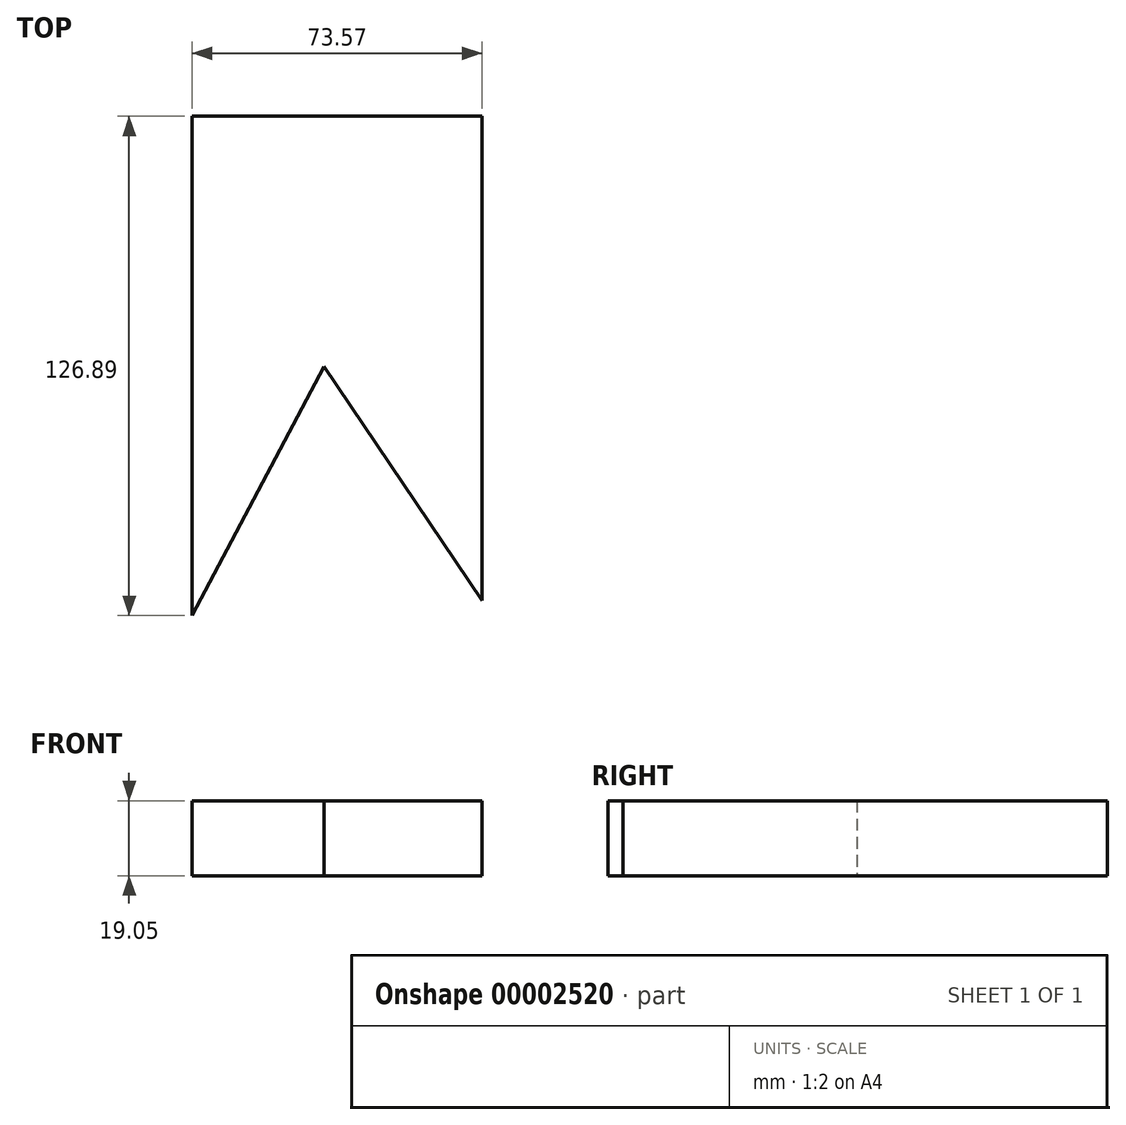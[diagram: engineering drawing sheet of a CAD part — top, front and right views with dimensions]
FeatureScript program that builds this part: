
annotation { "Feature Type Name" : "Feature", "Feature Type Description" : "" }
export const myFeature = defineFeature(function(context is Context, id is Id, definition is map)
    precondition{}
    {
        {
            var Q0;
            Q0=qCreatedBy(makeId("Top.planeOp"),FACE);
            var sketch = newSketch(context, id + "F0", { "sketchPlane" : qUnion([Q0])});
            skLineSegment(sketch, "E0", {"start": v(-237.79, 256.38) * mm, "end": v(-38.32, -319.66) * mm, "construction": true});
            skCircle(sketch, "E1", {"center": v(-237.79, 256.38) * mm, "radius": 22.23 * mm, "construction": true});
            skCircle(sketch, "E2", {"center": v(-38.32, -319.66) * mm, "radius": 22.23 * mm, "construction": true});
            skSolve(sketch);
        }
        {
            var Q0;
            Q0=qCreatedBy(makeId("Top.planeOp"),FACE);
            var sketch = newSketch(context, id + "F1", { "sketchPlane" : qUnion([Q0])});
            skLineSegment(sketch, "E3", {"start": v(-273.6, 236.28) * mm, "end": v(-240.07, 299.53) * mm});
            skLineSegment(sketch, "E4", {"start": v(-240.07, 299.53) * mm, "end": v(-200.03, 240.13) * mm});
            skLineSegment(sketch, "E5", {"start": v(-200.03, 240.13) * mm, "end": v(-200.03, 363.17) * mm});
            skLineSegment(sketch, "E6", {"start": v(-200.03, 363.17) * mm, "end": v(-273.6, 363.17) * mm});
            skLineSegment(sketch, "E7", {"start": v(-273.6, 363.17) * mm, "end": v(-273.6, 236.28) * mm});
            skSolve(sketch);
        }
        {
            var Q0;
            Q0 = qSketchRegion(id + "F1", true);
            extrude(context, id + "F2", {"entities" : qUnion([Q0]), "depth" : 19.05 * mm});
        }
        {
            var Q0;
            Q0=qCreatedBy(makeId("Top.planeOp"),FACE);
            cPlane(context, id + "F3", {"entities" : qUnion([Q0]), "cplaneType" : CPlaneType.OFFSET, "offset" : 355.6 * mm, "width" : 152.4 * mm, "height" : 152.4 * mm});
        }
        {
            var Q0;
            Q0=qCreatedBy(makeId("Top.planeOp"),FACE);
            var Q1;
            Q1=qCreatedBy(id+"F3.planeOp",FACE);
            cPlane(context, id + "F4", {"entities" : qUnion([Q0, Q1]), "cplaneType" : CPlaneType.MID_PLANE, "offset" : 25.4 * mm, "width" : 152.4 * mm, "height" : 152.4 * mm});
        }
    });
